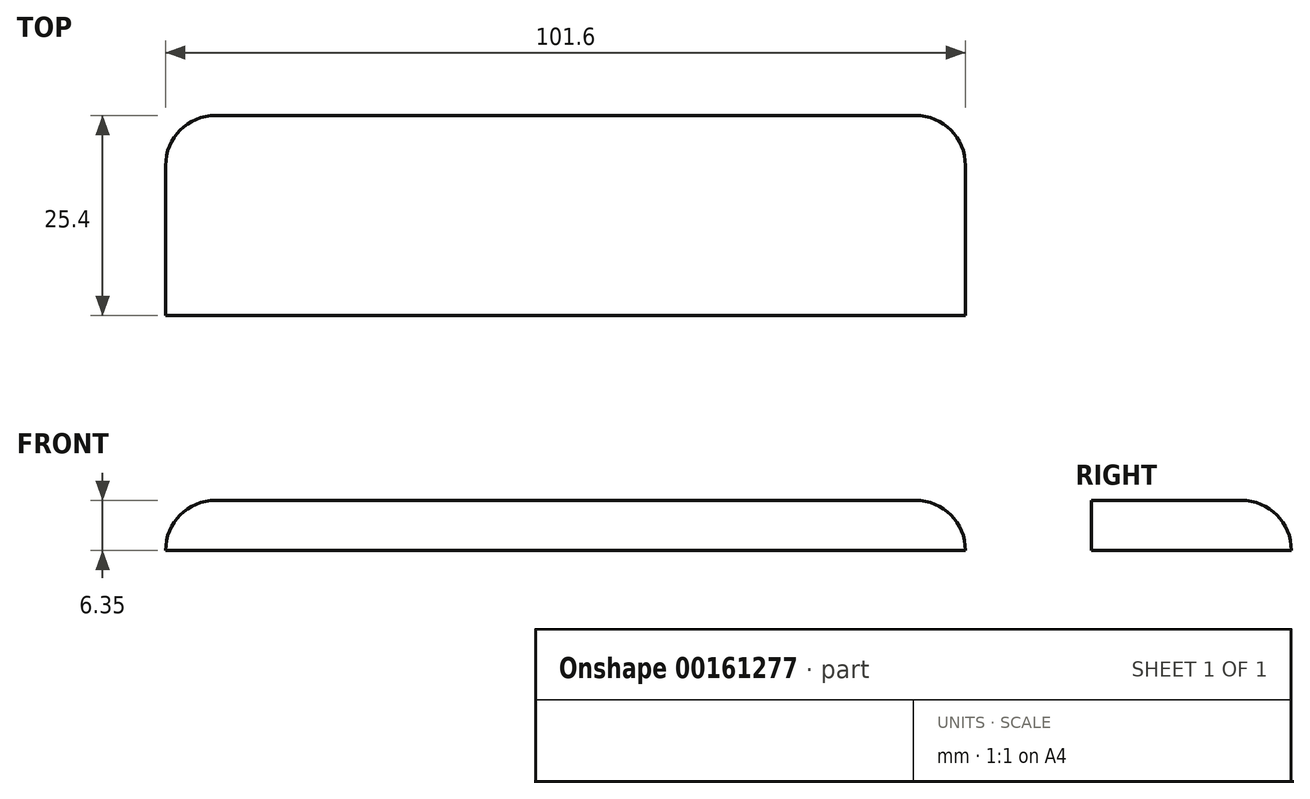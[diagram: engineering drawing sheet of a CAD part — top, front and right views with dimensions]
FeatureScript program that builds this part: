
annotation { "Feature Type Name" : "Feature", "Feature Type Description" : "" }
export const myFeature = defineFeature(function(context is Context, id is Id, definition is map)
    precondition{}
    {
        {
            var Q0;
            Q0=qCreatedBy(makeId("Top.planeOp"),FACE);
            var sketch = newSketch(context, id + "F0", { "sketchPlane" : qUnion([Q0])});
            skLineSegment(sketch, "E0.bottom", {"start": v(44.45, 12.7) * mm, "end": v(-44.45, 12.7) * mm});
            skLineSegment(sketch, "E0.top", {"start": v(50.8, -12.7) * mm, "end": v(-50.8, -12.7) * mm});
            skLineSegment(sketch, "E0.left", {"start": v(50.8, 6.35) * mm, "end": v(50.8, -12.7) * mm});
            skLineSegment(sketch, "E0.right", {"start": v(-50.8, 6.35) * mm, "end": v(-50.8, -12.7) * mm});
            skPoint(sketch, "E0.middle", {"position": v(0, 0) * mm});
            skPoint(sketch, "E1.visualSharp", {"position": v(-50.8, 12.7) * mm});
            skArc(sketch, "E1.filletArc", {"start": v(-44.45, 12.7) * mm, "mid": v(-48.94, 10.84) * mm, "end": v(-50.8, 6.35) * mm});
            skPoint(sketch, "E2.visualSharp", {"position": v(50.8, 12.7) * mm});
            skArc(sketch, "E2.filletArc", {"start": v(50.8, 6.35) * mm, "mid": v(48.94, 10.84) * mm, "end": v(44.45, 12.7) * mm});
            skSolve(sketch);
        }
        {
            var Q0;
            Q0=makeQuery(id+"F0.imprint","IMPRINT",FACE,{"disambiguationData":[TD([[makeQuery(id+"F0.imprint","IMPRINT",EDGE,{"derivedFrom":sQuery(id+"F0.wireOp",EDGE,"E0.bottom")}),1.0]])]});
            extrude(context, id + "F1", {"entities" : qUnion([Q0]), "depth" : 6.35 * mm});
        }
        {
            var Q0;
            Q0=makeQuery(id+"F1.opExtrude","CAP_EDGE",EDGE,{"disambiguationData":[OSD([sQuery(id+"F0.wireOp",EDGE,"E0.bottom")])],"isStart":false});
            fillet(context, id + "F2", {"entities" : qUnion([Q0]), "radius" : 6.35 * mm, "tangentPropagation" : true, "allowEdgeOverflow" : false});
        }
    });
